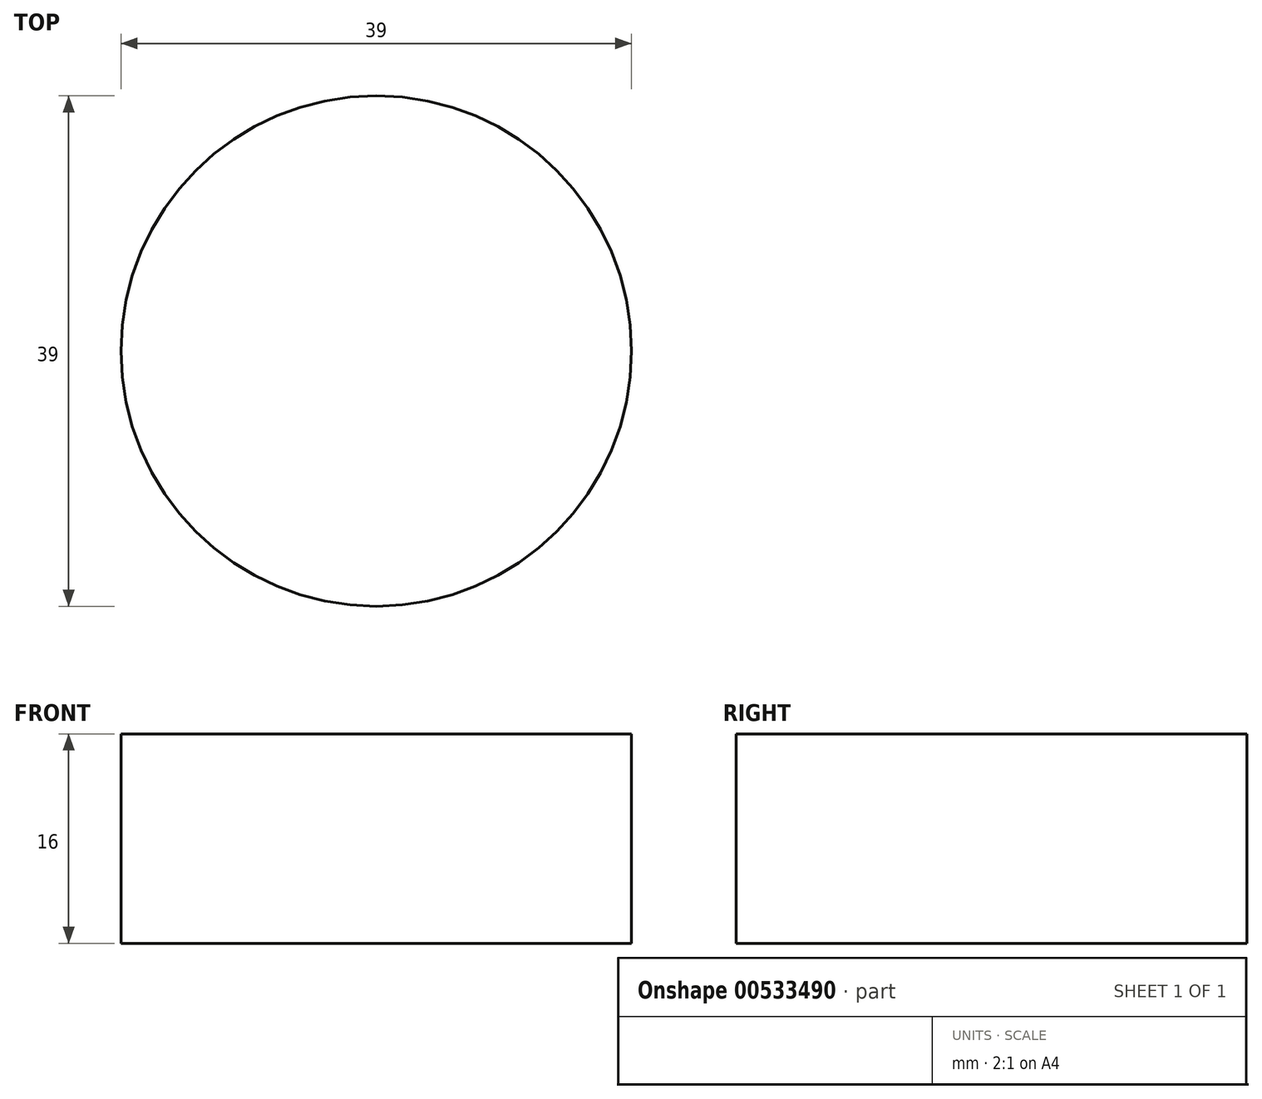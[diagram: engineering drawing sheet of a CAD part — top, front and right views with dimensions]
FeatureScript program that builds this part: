
annotation { "Feature Type Name" : "Feature", "Feature Type Description" : "" }
export const myFeature = defineFeature(function(context is Context, id is Id, definition is map)
    precondition{}
    {
        {
            var Q0;
            Q0=qCreatedBy(makeId("Top.planeOp"),FACE);
            var sketch = newSketch(context, id + "F0", { "sketchPlane" : qUnion([Q0])});
            skCircle(sketch, "E0", {"center": v(0, 0) * mm, "radius": 19.5 * mm});
            skSolve(sketch);
        }
        {
            var Q0;
            Q0 = qSketchRegion(id + "F0", true);
            extrude(context, id + "F1", {"entities" : qUnion([Q0]), "depth" : 16 * mm, "offsetDistance" : 25 * mm});
        }
    });
